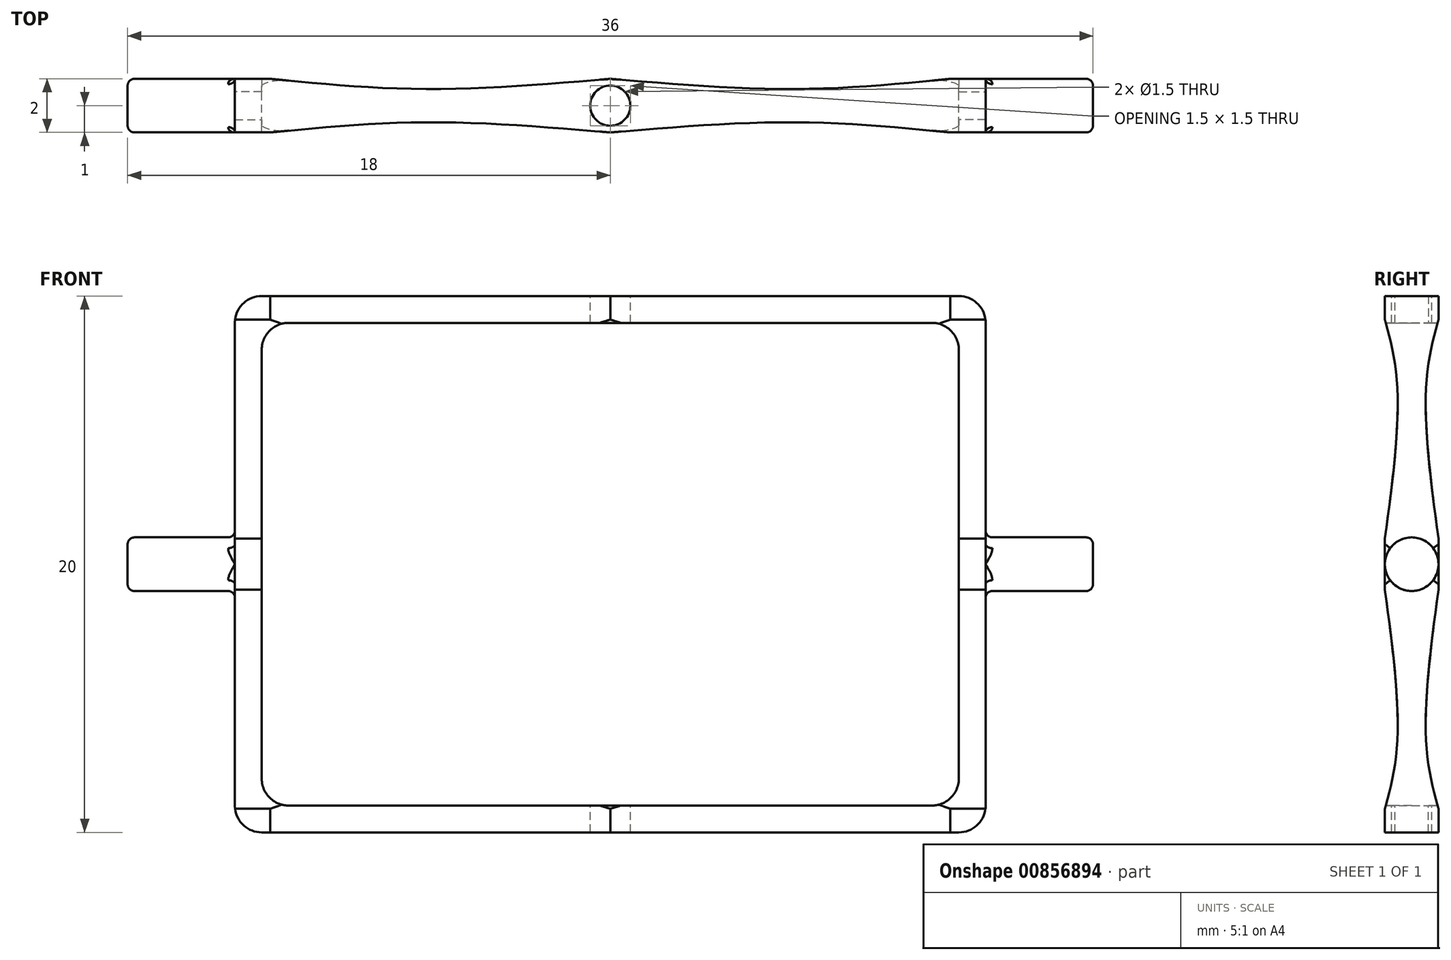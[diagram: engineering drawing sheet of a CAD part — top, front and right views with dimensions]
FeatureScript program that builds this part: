
annotation { "Feature Type Name" : "Feature", "Feature Type Description" : "" }
export const myFeature = defineFeature(function(context is Context, id is Id, definition is map)
    precondition{}
    {
        {
            var Q0;
            Q0=qCreatedBy(makeId("Front.planeOp"),FACE);
            var sketch = newSketch(context, id + "F0", { "sketchPlane" : qUnion([Q0])});
            skLineSegment(sketch, "E0", {"start": v(0, 0) * mm, "end": v(14, 0) * mm});
            skLineSegment(sketch, "E1", {"start": v(14, 0) * mm, "end": v(14, 20) * mm});
            skLineSegment(sketch, "E2", {"start": v(14, 20) * mm, "end": v(0, 20) * mm});
            skLineSegment(sketch, "E3", {"start": v(0, 20) * mm, "end": v(0, 19) * mm});
            skLineSegment(sketch, "E4", {"start": v(0, 19) * mm, "end": v(13, 19) * mm});
            skLineSegment(sketch, "E5", {"start": v(13, 19) * mm, "end": v(13, 1) * mm});
            skLineSegment(sketch, "E6", {"start": v(13, 1) * mm, "end": v(0, 1) * mm});
            skLineSegment(sketch, "E7", {"start": v(0, 1) * mm, "end": v(0, 0) * mm});
            skSolve(sketch);
        }
        {
            var Q0;
            Q0=makeQuery(id+"F0.imprint","IMPRINT",FACE,{"disambiguationData":[TD([[makeQuery(id+"F0.imprint","IMPRINT",EDGE,{"derivedFrom":sQuery(id+"F0.wireOp",EDGE,"E0")}),1.0]])]});
            extrude(context, id + "F1", {"entities" : qUnion([Q0]), "endBound" : BoundingType.SYMMETRIC, "depth" : 2 * mm, "offsetDistance" : 25 * mm});
        }
        {
            var Q0;
            Q0=makeQuery(id+"F1.opExtrude","SWEPT_FACE",FACE,{"disambiguationData":[OSD([sQuery(id+"F0.wireOp",EDGE,"E1")])]});
            var sketch = newSketch(context, id + "F2", { "sketchPlane" : qUnion([Q0])});
            skCircle(sketch, "E8", {"center": v(0, 10) * mm, "radius": 1 * mm});
            skSolve(sketch);
        }
        {
            var Q0;
            {var subQ0=sQuery(id+"F2.wireOp",EDGE,"E8");var subQ1=sQuery(id+"F0.wireOp",EDGE,"E1");var subQ2=makeQuery(id+"F2.imprint","INTERSECT",VERTEX,{"derivedFrom":[makeQuery(id+"F1.opExtrude","CAP_EDGE",EDGE,{"disambiguationData":[OSD([subQ1])],"isStart":true}),subQ0]});Q0=makeQuery(id+"F2.imprint","IMPRINT",FACE,{"disambiguationData":[TD([[makeQuery(id+"F2.imprint","IMPRINT",EDGE,{"disambiguationData":[TD([[subQ2,-1.0]])],"derivedFrom":subQ0}),1.0]])]});}
            extrude(context, id + "F3", {"entities" : qUnion([Q0]), "operationType" : NewBodyOperationType.ADD, "depth" : 4 * mm, "offsetDistance" : 25 * mm});
        }
        {
            var Q0;
            Q0=makeQuery(id+"F3.boolean.opBoolean","SPLIT",EDGE,{"disambiguationData":[OD(1.0)],"derivedFrom":makeQuery(id+"F3.opExtrude","CAP_EDGE",EDGE,{"disambiguationData":[OSD([sQuery(id+"F2.wireOp",EDGE,"E8")])],"isStart":true})});
            var Q1;
            Q1=makeQuery(id+"F3.opExtrude","CAP_EDGE",EDGE,{"disambiguationData":[OSD([sQuery(id+"F2.wireOp",EDGE,"E8")])],"isStart":false});
            fillet(context, id + "F4", {"entities" : qUnion([Q0, Q1]), "radius" : 0.25 * mm, "tangentPropagation" : true, "allowEdgeOverflow" : false});
        }
        {
            var Q0;
            {var subQ0=sQuery(id+"F0.wireOp",EDGE,"E1");var subQ1=makeQuery(id+"F1.opExtrude","SWEPT_FACE",FACE,{"disambiguationData":[OSD([subQ0])]});var subQ8=sQuery(id+"F0.wireOp",EDGE,"E0");Q0=makeQuery(id+"F3.boolean.opBoolean","SPLIT",FACE,{"disambiguationData":[TD([makeQuery(id+"F1.opExtrude","SWEPT_FACE",FACE,{"disambiguationData":[OSD([subQ8])]})])],"derivedFrom":subQ1});}
            var sketch = newSketch(context, id + "F5", { "sketchPlane" : qUnion([Q0])});
            skFitSpline(sketch, "E9", {"points": [v(-1, 9.04) * mm, v(-0.53, 3.44) * mm, v(-1, 0.88) * mm], "startDerivative": vector(1.36, -9.8) * mm, "endDerivative": vector(-1.53, -5.65) * mm});
            skLineSegment(sketch, "E10", {"start": v(-1, 0.88) * mm, "end": v(-1, 9.04) * mm});
            skFitSpline(sketch, "E11.MirrorCS", {"points": [v(1, 9.04) * mm, v(0.53, 3.44) * mm, v(1, 0.88) * mm], "startDerivative": vector(-1.36, -9.8) * mm, "endDerivative": vector(1.53, -5.65) * mm});
            skLineSegment(sketch, "E12.MirrorCS", {"start": v(1, 0.88) * mm, "end": v(1, 9.04) * mm});
            skLineSegment(sketch, "E13", {"start": v(-9.16, 10) * mm, "end": v(11.19, 10) * mm, "construction": true});
            skFitSpline(sketch, "E14.MirrorCS", {"points": [v(-1, 10.96) * mm, v(-0.53, 16.56) * mm, v(-1, 19.12) * mm], "startDerivative": vector(1.36, 9.8) * mm, "endDerivative": vector(-1.53, 5.65) * mm});
            skLineSegment(sketch, "E15.MirrorCS", {"start": v(-1, 19.12) * mm, "end": v(-1, 10.96) * mm});
            skFitSpline(sketch, "E16.MirrorCS", {"points": [v(1, 10.96) * mm, v(0.53, 16.56) * mm, v(1, 19.12) * mm], "startDerivative": vector(-1.36, 9.8) * mm, "endDerivative": vector(1.53, 5.65) * mm});
            skLineSegment(sketch, "E17.MirrorCS", {"start": v(1, 19.12) * mm, "end": v(1, 10.96) * mm});
            skSolve(sketch);
        }
        {
            var Q0;
            Q0=makeQuery(id+"F5.imprint","IMPRINT",FACE,{"disambiguationData":[TD([[makeQuery(id+"F5.imprint","IMPRINT",EDGE,{"derivedFrom":sQuery(id+"F5.wireOp",EDGE,"E9")}),-1.0]])]});
            var Q1;
            Q1=makeQuery(id+"F5.imprint","IMPRINT",FACE,{"disambiguationData":[TD([[makeQuery(id+"F5.imprint","IMPRINT",EDGE,{"derivedFrom":sQuery(id+"F5.wireOp",EDGE,"E11.MirrorCS")}),1.0]])]});
            extrude(context, id + "F6", {"entities" : qUnion([Q0, Q1]), "operationType" : NewBodyOperationType.REMOVE, "endBound" : BoundingType.THROUGH_ALL, "oppositeDirection" : true, "depth" : 25 * mm, "offsetDistance" : 25 * mm});
        }
        {
            var Q0;
            Q0 = qSketchRegion(id + "F5", true);
            extrude(context, id + "F7", {"entities" : qUnion([Q0]), "operationType" : NewBodyOperationType.REMOVE, "endBound" : BoundingType.THROUGH_ALL, "oppositeDirection" : true, "depth" : 25 * mm, "offsetDistance" : 25 * mm});
        }
        {
            var Q0;
            Q0=makeQuery(id+"F1.opExtrude","SWEPT_BODY",BODY,{"disambiguationData":[OSD([sQuery(id+"F0.wireOp",EDGE,"E0"),sQuery(id+"F0.wireOp",EDGE,"E1"),sQuery(id+"F0.wireOp",EDGE,"E2"),sQuery(id+"F0.wireOp",EDGE,"E3"),sQuery(id+"F0.wireOp",EDGE,"E4"),sQuery(id+"F0.wireOp",EDGE,"E5"),sQuery(id+"F0.wireOp",EDGE,"E6"),sQuery(id+"F0.wireOp",EDGE,"E7")])]});
            var Q1;
            Q1=qCreatedBy(makeId("Right.planeOp"),FACE);
            mirror(context, id + "F8", {"operationType" : NewBodyOperationType.ADD, "entities" : qUnion([Q0]), "mirrorPlane" : qUnion([Q1])});
        }
        {
            var Q0;
            {var subQ0=makeQuery(id+"F1.opExtrude","SWEPT_FACE",FACE,{"disambiguationData":[OSD([sQuery(id+"F0.wireOp",EDGE,"E6")])]});Q0=makeQuery(id+"F8.boolean.opBoolean","MERGE",FACE,{"derivedFrom":[subQ0,makeQuery(id+"F8.opPattern","COPY",FACE,{"derivedFrom":subQ0,"instanceName":"1"})]});}
            var sketch = newSketch(context, id + "F9", { "sketchPlane" : qUnion([Q0])});
            skCircle(sketch, "E18", {"center": v(0, 0) * mm, "radius": 0.75 * mm});
            skSolve(sketch);
        }
        {
            var Q0;
            Q0=makeQuery(id+"F9.imprint","IMPRINT",FACE,{"disambiguationData":[TD([[makeQuery(id+"F9.imprint","IMPRINT",EDGE,{"derivedFrom":sQuery(id+"F9.wireOp",EDGE,"E18")}),1.0]])]});
            extrude(context, id + "F10", {"entities" : qUnion([Q0]), "operationType" : NewBodyOperationType.REMOVE, "endBound" : BoundingType.THROUGH_ALL, "oppositeDirection" : true, "depth" : 25 * mm, "offsetDistance" : 25 * mm, "hasSecondDirection" : true, "secondDirectionBound" : SecondDirectionBoundingType.THROUGH_ALL, "secondDirectionOppositeDirection" : false, "secondDirectionDepth" : 25 * mm});
        }
        {
            var Q0;
            {var subQ0=makeQuery(id+"F1.opExtrude","SWEPT_FACE",FACE,{"disambiguationData":[OSD([sQuery(id+"F0.wireOp",EDGE,"E2")])]});Q0=makeQuery(id+"F8.boolean.opBoolean","MERGE",FACE,{"derivedFrom":[subQ0,makeQuery(id+"F8.opPattern","COPY",FACE,{"derivedFrom":subQ0,"instanceName":"1"})]});}
            var sketch = newSketch(context, id + "F11", { "sketchPlane" : qUnion([Q0])});
            skFitSpline(sketch, "E19", {"points": [v(-12.68, 1) * mm, v(-6.85, 0.62) * mm, v(0, 1) * mm], "startDerivative": vector(11.9, -1.16) * mm, "endDerivative": vector(13.44, 1.13) * mm});
            skLineSegment(sketch, "E20", {"start": v(-12.68, 1) * mm, "end": v(0, 1) * mm});
            skFitSpline(sketch, "E21.MirrorCS", {"points": [v(-12.68, -1) * mm, v(-6.85, -0.62) * mm, v(0, -1) * mm], "startDerivative": vector(11.9, 1.16) * mm, "endDerivative": vector(13.44, -1.13) * mm});
            skLineSegment(sketch, "E22.MirrorCS", {"start": v(-12.68, -1) * mm, "end": v(0, -1) * mm});
            skFitSpline(sketch, "E23.MirrorCS", {"points": [v(12.68, 1) * mm, v(6.85, 0.62) * mm, v(0, 1) * mm], "startDerivative": vector(-11.9, -1.16) * mm, "endDerivative": vector(-13.44, 1.13) * mm});
            skLineSegment(sketch, "E24.MirrorCS", {"start": v(12.68, 1) * mm, "end": v(0, 1) * mm});
            skFitSpline(sketch, "E25.MirrorCS", {"points": [v(12.68, -1) * mm, v(6.85, -0.62) * mm, v(0, -1) * mm], "startDerivative": vector(-11.9, 1.16) * mm, "endDerivative": vector(-13.44, -1.13) * mm});
            skLineSegment(sketch, "E26.MirrorCS", {"start": v(12.68, -1) * mm, "end": v(0, -1) * mm});
            skSolve(sketch);
        }
        {
            var Q0;
            Q0=makeQuery(id+"F11.imprint","IMPRINT",FACE,{"disambiguationData":[TD([[makeQuery(id+"F11.imprint","IMPRINT",EDGE,{"derivedFrom":sQuery(id+"F11.wireOp",EDGE,"E19")}),1.0]])]});
            var Q1;
            Q1=makeQuery(id+"F11.imprint","IMPRINT",FACE,{"disambiguationData":[TD([[makeQuery(id+"F11.imprint","IMPRINT",EDGE,{"derivedFrom":sQuery(id+"F11.wireOp",EDGE,"E21.MirrorCS")}),-1.0]])]});
            var Q2;
            Q2=makeQuery(id+"F11.imprint","IMPRINT",FACE,{"disambiguationData":[TD([[makeQuery(id+"F11.imprint","IMPRINT",EDGE,{"derivedFrom":sQuery(id+"F11.wireOp",EDGE,"E25.MirrorCS")}),1.0]])]});
            var Q3;
            Q3=makeQuery(id+"F11.imprint","IMPRINT",FACE,{"disambiguationData":[TD([[makeQuery(id+"F11.imprint","IMPRINT",EDGE,{"derivedFrom":sQuery(id+"F11.wireOp",EDGE,"E23.MirrorCS")}),-1.0]])]});
            extrude(context, id + "F12", {"entities" : qUnion([Q0, Q1, Q2, Q3]), "operationType" : NewBodyOperationType.REMOVE, "endBound" : BoundingType.THROUGH_ALL, "oppositeDirection" : true, "depth" : 25 * mm, "offsetDistance" : 25 * mm});
        }
        {
            var Q0;
            Q0=makeQuery(id+"F8.opPattern","COPY",EDGE,{"derivedFrom":makeQuery(id+"F1.opExtrude","SWEPT_EDGE",EDGE,{"disambiguationData":[OSD([sQuery(id+"F0.wireOp",EDGE,"E0"),sQuery(id+"F0.wireOp",EDGE,"E1")])]}),"instanceName":"1"});
            var Q1;
            Q1=makeQuery(id+"F8.opPattern","COPY",EDGE,{"derivedFrom":makeQuery(id+"F1.opExtrude","SWEPT_EDGE",EDGE,{"disambiguationData":[OSD([sQuery(id+"F0.wireOp",EDGE,"E5"),sQuery(id+"F0.wireOp",EDGE,"E6")])]}),"instanceName":"1"});
            var Q2;
            Q2=makeQuery(id+"F1.opExtrude","SWEPT_EDGE",EDGE,{"disambiguationData":[OSD([sQuery(id+"F0.wireOp",EDGE,"E5"),sQuery(id+"F0.wireOp",EDGE,"E6")])]});
            var Q3;
            Q3=makeQuery(id+"F1.opExtrude","SWEPT_EDGE",EDGE,{"disambiguationData":[OSD([sQuery(id+"F0.wireOp",EDGE,"E0"),sQuery(id+"F0.wireOp",EDGE,"E1")])]});
            var Q4;
            Q4=makeQuery(id+"F1.opExtrude","SWEPT_EDGE",EDGE,{"disambiguationData":[OSD([sQuery(id+"F0.wireOp",EDGE,"E1"),sQuery(id+"F0.wireOp",EDGE,"E2")])]});
            var Q5;
            Q5=makeQuery(id+"F1.opExtrude","SWEPT_EDGE",EDGE,{"disambiguationData":[OSD([sQuery(id+"F0.wireOp",EDGE,"E4"),sQuery(id+"F0.wireOp",EDGE,"E5")])]});
            var Q6;
            Q6=makeQuery(id+"F8.opPattern","COPY",EDGE,{"derivedFrom":makeQuery(id+"F1.opExtrude","SWEPT_EDGE",EDGE,{"disambiguationData":[OSD([sQuery(id+"F0.wireOp",EDGE,"E4"),sQuery(id+"F0.wireOp",EDGE,"E5")])]}),"instanceName":"1"});
            var Q7;
            Q7=makeQuery(id+"F8.opPattern","COPY",EDGE,{"derivedFrom":makeQuery(id+"F1.opExtrude","SWEPT_EDGE",EDGE,{"disambiguationData":[OSD([sQuery(id+"F0.wireOp",EDGE,"E1"),sQuery(id+"F0.wireOp",EDGE,"E2")])]}),"instanceName":"1"});
            fillet(context, id + "F13", {"entities" : qUnion([Q0, Q1, Q2, Q3, Q4, Q5, Q6, Q7]), "radius" : 1 * mm, "tangentPropagation" : true, "allowEdgeOverflow" : false});
        }
    });
